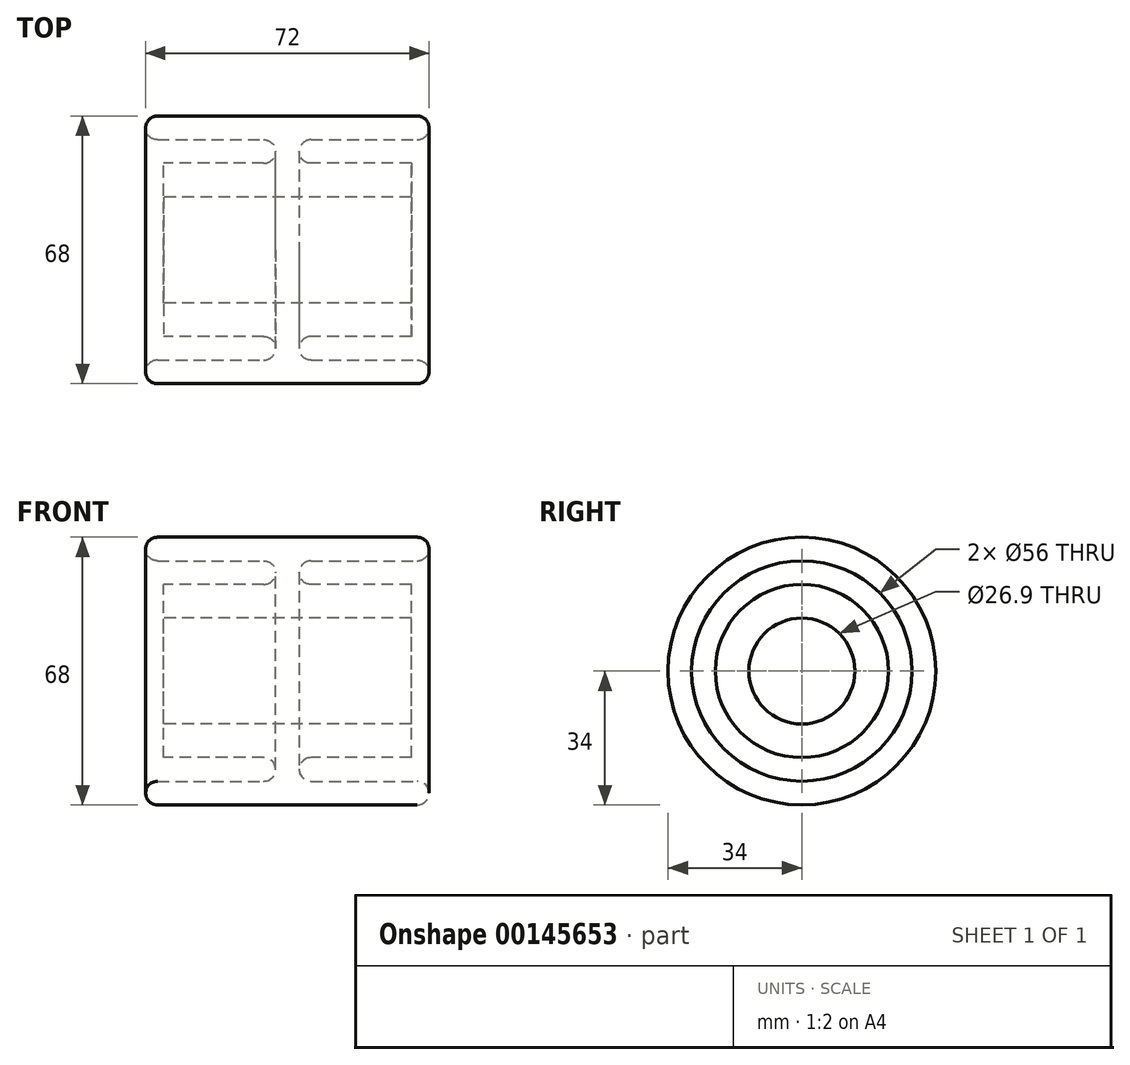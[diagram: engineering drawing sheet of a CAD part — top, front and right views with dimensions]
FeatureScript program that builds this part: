
annotation { "Feature Type Name" : "Feature", "Feature Type Description" : "" }
export const myFeature = defineFeature(function(context is Context, id is Id, definition is map)
    precondition{}
    {
        {
            var Q0;
            Q0=qCreatedBy(makeId("Right.planeOp"),FACE);
            var sketch = newSketch(context, id + "F0", { "sketchPlane" : qUnion([Q0])});
            skCircle(sketch, "E0", {"center": v(0, 0) * mm, "radius": 13.45 * mm});
            skCircle(sketch, "E1", {"center": v(0, 0) * mm, "radius": 22 * mm});
            skSolve(sketch);
        }
        {
            var Q0;
            Q0=qSketchRegion(id+"F0",true);
            extrude(context, id + "F1", {"entities" : qUnion([Q0]), "depth" : 63 * mm});
        }
        {
            var Q0;
            Q0=qCreatedBy(makeId("Front.planeOp"),FACE);
            var sketch = newSketch(context, id + "F2", { "sketchPlane" : qUnion([Q0])});
            skLineSegment(sketch, "E2", {"start": v(31.5, 0) * mm, "end": v(31.5, 25.59) * mm, "construction": true});
            skLineSegment(sketch, "E3", {"start": v(-1.5, 34) * mm, "end": v(64.5, 34) * mm});
            skArc(sketch, "E4", {"start": v(-1.5, 34) * mm, "mid": v(-4.5, 31) * mm, "end": v(-1.5, 28) * mm});
            skArc(sketch, "E5", {"start": v(64.5, 34) * mm, "mid": v(67.5, 31) * mm, "end": v(64.5, 28) * mm});
            skLineSegment(sketch, "E6", {"start": v(-1.5, 28) * mm, "end": v(25.5, 28) * mm});
            skLineSegment(sketch, "E7", {"start": v(64.5, 28) * mm, "end": v(37.5, 28) * mm});
            skLineSegment(sketch, "E8", {"start": v(0, 22) * mm, "end": v(63, 22) * mm, "construction": true});
            skArc(sketch, "E9", {"start": v(25.5, 28) * mm, "mid": v(28.5, 25) * mm, "end": v(25.5, 22) * mm});
            skArc(sketch, "E10", {"start": v(37.5, 28) * mm, "mid": v(34.5, 25) * mm, "end": v(37.5, 22) * mm});
            skLineSegment(sketch, "E11", {"start": v(25.5, 22) * mm, "end": v(37.5, 22) * mm});
            skSolve(sketch);
        }
        {
            var Q0;
            Q0=qSketchRegion(id+"F2",true);
            var Q1;
            Q1=makeQuery(id+"F1.opExtrude","SWEPT_FACE",FACE,{"disambiguationData":[OSD([sQuery(id+"F0.wireOp",EDGE,"E1")])]});
            revolve(context, id + "F3", {"operationType" : NewBodyOperationType.ADD, "entities" : qUnion([Q0]), "axis" : qUnion([Q1]), "revolveType" : RevolveType.FULL});
        }
    });
